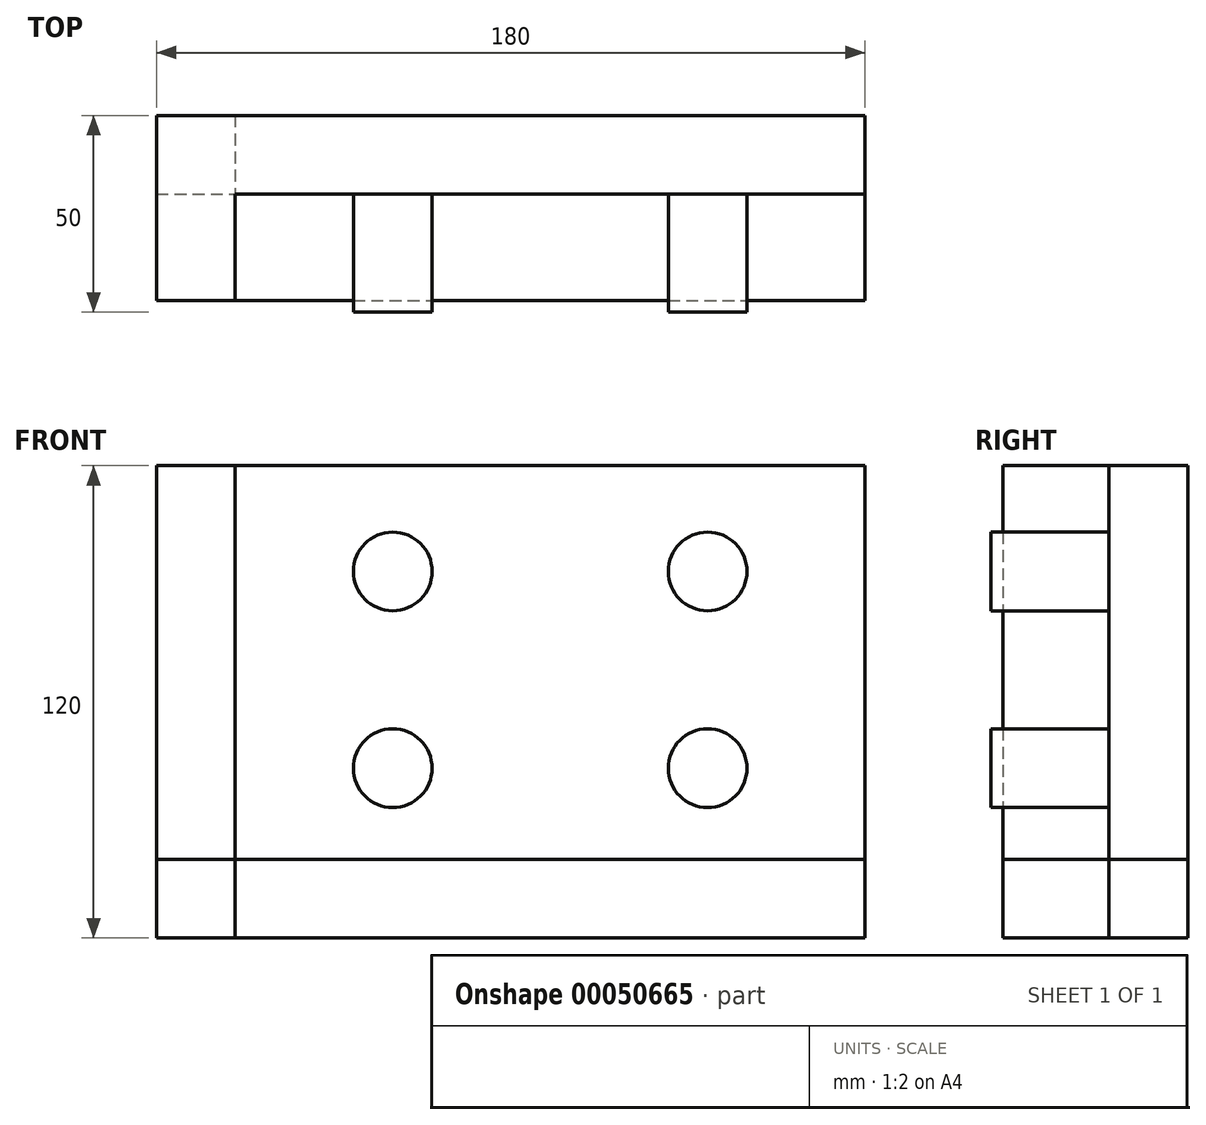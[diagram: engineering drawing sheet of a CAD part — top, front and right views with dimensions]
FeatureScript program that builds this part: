
annotation { "Feature Type Name" : "Feature", "Feature Type Description" : "" }
export const myFeature = defineFeature(function(context is Context, id is Id, definition is map)
    precondition{}
    {
        {
            var Q0;
            Q0=qCreatedBy(makeId("Front.planeOp"),FACE);
            var sketch = newSketch(context, id + "F0", { "sketchPlane" : qUnion([Q0])});
            skLineSegment(sketch, "E0.bottom", {"start": v(-80, 50) * mm, "end": v(80, 50) * mm});
            skLineSegment(sketch, "E0.top", {"start": v(-80, -50) * mm, "end": v(80, -50) * mm});
            skLineSegment(sketch, "E0.left", {"start": v(-80, 50) * mm, "end": v(-80, -50) * mm});
            skLineSegment(sketch, "E0.right", {"start": v(80, 50) * mm, "end": v(80, -50) * mm});
            skSolve(sketch);
        }
        {
            var Q0;
            Q0=makeQuery(id+"F0.imprint","IMPRINT",FACE,{"disambiguationData":[TD([[makeQuery(id+"F0.imprint","IMPRINT",EDGE,{"derivedFrom":sQuery(id+"F0.wireOp",EDGE,"E0.bottom")}),-1.0]])]});
            extrude(context, id + "F1", {"entities" : qUnion([Q0]), "oppositeDirection" : true, "depth" : 20 * mm});
        }
        {
            var Q0;
            Q0=qCreatedBy(makeId("Right.planeOp"),FACE);
            cPlane(context, id + "F2", {"entities" : qUnion([Q0]), "cplaneType" : CPlaneType.OFFSET, "offset" : 80 * mm, "oppositeDirection" : true, "width" : 150 * mm, "height" : 150 * mm});
        }
        {
            var Q0;
            Q0=qCreatedBy(id+"F2.planeOp",FACE);
            var sketch = newSketch(context, id + "F3", { "sketchPlane" : qUnion([Q0])});
            skLineSegment(sketch, "E1.bottom", {"start": v(-27, 50) * mm, "end": v(0, 50) * mm});
            skLineSegment(sketch, "E1.top", {"start": v(-27, -50) * mm, "end": v(0, -50) * mm});
            skLineSegment(sketch, "E1.left", {"start": v(-27, 50) * mm, "end": v(-27, -50) * mm});
            skLineSegment(sketch, "E1.right", {"start": v(0, 50) * mm, "end": v(0, -50) * mm});
            skSolve(sketch);
        }
        {
            var Q0;
            Q0=makeQuery(id+"F3.imprint","IMPRINT",FACE,{"disambiguationData":[TD([[makeQuery(id+"F3.imprint","IMPRINT",EDGE,{"derivedFrom":sQuery(id+"F3.wireOp",EDGE,"E1.bottom")}),-1.0]])]});
            extrude(context, id + "F4", {"entities" : qUnion([Q0]), "operationType" : NewBodyOperationType.ADD, "oppositeDirection" : true, "depth" : 20 * mm});
        }
        {
            var Q0;
            Q0=makeQuery(id+"F4.opExtrude","SWEPT_FACE",FACE,{"disambiguationData":[OSD([sQuery(id+"F3.wireOp",EDGE,"E1.left")])]});
            var Q1;
            Q1=makeQuery(id+"F4.opExtrude","SWEPT_FACE",FACE,{"disambiguationData":[OSD([sQuery(id+"F3.wireOp",EDGE,"E1.right")])]});
            extrude(context, id + "F5", {"entities" : qUnion([Q0, Q1]), "operationType" : NewBodyOperationType.ADD, "oppositeDirection" : true, "depth" : 20 * mm});
        }
        {
            var Q0;
            Q0=makeQuery(id+"F1.opExtrude","CAP_FACE",FACE,{"disambiguationData":[OSD([sQuery(id+"F0.wireOp",EDGE,"E0.bottom"),sQuery(id+"F0.wireOp",EDGE,"E0.top"),sQuery(id+"F0.wireOp",EDGE,"E0.left"),sQuery(id+"F0.wireOp",EDGE,"E0.right")])],"isStart":true});
            var sketch = newSketch(context, id + "F6", { "sketchPlane" : qUnion([Q0])});
            skCircle(sketch, "E2", {"center": v(-40, -26.85) * mm, "radius": 10 * mm});
            skCircle(sketch, "E3.0.1.0", {"center": v(-40, 23.15) * mm, "radius": 10 * mm});
            skCircle(sketch, "E3.1.0.0", {"center": v(40, -26.85) * mm, "radius": 10 * mm});
            skCircle(sketch, "E3.1.1.0", {"center": v(40, 23.15) * mm, "radius": 10 * mm});
            skLineSegment(sketch, "E3.direction1", {"start": v(-40, -26.85) * mm, "end": v(40, -26.85) * mm, "construction": true});
            skLineSegment(sketch, "E3.direction2", {"start": v(-40, -26.85) * mm, "end": v(-40, 23.15) * mm, "construction": true});
            skSolve(sketch);
        }
        {
            var Q0;
            Q0=qSketchRegion(id+"F6",true);
            extrude(context, id + "F7", {"entities" : qUnion([Q0]), "operationType" : NewBodyOperationType.ADD, "depth" : 30 * mm});
        }
        {
            var Q0;
            Q0=qCreatedBy(makeId("Top.planeOp"),FACE);
            cPlane(context, id + "F8", {"entities" : qUnion([Q0]), "cplaneType" : CPlaneType.OFFSET, "offset" : 50 * mm, "oppositeDirection" : true, "width" : 150 * mm, "height" : 150 * mm});
        }
        {
            var Q0;
            Q0=qCreatedBy(id+"F8.planeOp",FACE);
            var sketch = newSketch(context, id + "F9", { "sketchPlane" : qUnion([Q0])});
            skLineSegment(sketch, "E4.bottom", {"start": v(-80, 0) * mm, "end": v(80, 0) * mm});
            skLineSegment(sketch, "E4.top", {"start": v(-80, -27) * mm, "end": v(80, -27) * mm});
            skLineSegment(sketch, "E4.left", {"start": v(-80, 0) * mm, "end": v(-80, -27) * mm});
            skLineSegment(sketch, "E4.right", {"start": v(80, 0) * mm, "end": v(80, -27) * mm});
            skSolve(sketch);
        }
        {
            var Q0;
            Q0=makeQuery(id+"F9.imprint","IMPRINT",FACE,{"disambiguationData":[TD([[makeQuery(id+"F9.imprint","IMPRINT",EDGE,{"derivedFrom":sQuery(id+"F9.wireOp",EDGE,"E4.bottom")}),-1.0]])]});
            extrude(context, id + "F10", {"entities" : qUnion([Q0]), "oppositeDirection" : true, "depth" : 20 * mm});
        }
        {
            var Q0;
            Q0=makeQuery(id+"F10.opExtrude","SWEPT_FACE",FACE,{"disambiguationData":[OSD([sQuery(id+"F9.wireOp",EDGE,"E4.bottom")])]});
            var Q1;
            Q1=makeQuery(id+"F1.opExtrude","CAP_FACE",FACE,{"disambiguationData":[OSD([sQuery(id+"F0.wireOp",EDGE,"E0.bottom"),sQuery(id+"F0.wireOp",EDGE,"E0.top"),sQuery(id+"F0.wireOp",EDGE,"E0.left"),sQuery(id+"F0.wireOp",EDGE,"E0.right")])],"isStart":false});
            extrude(context, id + "F11", {"entities" : qUnion([Q0]), "endBound" : BoundingType.UP_TO_SURFACE, "endBoundEntityFace" : qUnion([Q1]), "depth" : 25 * mm});
        }
        {
            var Q0;
            Q0=makeQuery(id+"F10.opExtrude","SWEPT_FACE",FACE,{"disambiguationData":[OSD([sQuery(id+"F9.wireOp",EDGE,"E4.left")])]});
            var Q1;
            {var subQ0=sQuery(id+"F3.wireOp",EDGE,"E1.right");Q1=makeQuery(id+"F5.boolean.opBoolean","MERGE",FACE,{"derivedFrom":[makeQuery(id+"F4.opExtrude","CAP_FACE",FACE,{"disambiguationData":[OSD([sQuery(id+"F3.wireOp",EDGE,"E1.bottom"),sQuery(id+"F3.wireOp",EDGE,"E1.top"),sQuery(id+"F3.wireOp",EDGE,"E1.left"),subQ0])],"isStart":false}),makeQuery(id+"F5.opExtrude","SWEPT_FACE",FACE,{"disambiguationData":[OSD([subQ0]),TDD([makeQuery(id+"F4.opExtrude","CAP_EDGE",EDGE,{"disambiguationData":[OSD([subQ0])],"isStart":false})])]})]});}
            extrude(context, id + "F12", {"entities" : qUnion([Q0]), "endBound" : BoundingType.UP_TO_SURFACE, "endBoundEntityFace" : qUnion([Q1]), "depth" : 25 * mm});
        }
        {
            var Q0;
            Q0=makeQuery(id+"F11.opExtrude","SWEPT_FACE",FACE,{"disambiguationData":[OSD([sQuery(id+"F9.wireOp",EDGE,"E4.bottom"),sQuery(id+"F9.wireOp",EDGE,"E4.left")])]});
            var Q1;
            {var subQ0=sQuery(id+"F3.wireOp",EDGE,"E1.right");Q1=makeQuery(id+"F5.boolean.opBoolean","MERGE",FACE,{"derivedFrom":[makeQuery(id+"F4.opExtrude","CAP_FACE",FACE,{"disambiguationData":[OSD([sQuery(id+"F3.wireOp",EDGE,"E1.bottom"),sQuery(id+"F3.wireOp",EDGE,"E1.top"),sQuery(id+"F3.wireOp",EDGE,"E1.left"),subQ0])],"isStart":false}),makeQuery(id+"F5.opExtrude","SWEPT_FACE",FACE,{"disambiguationData":[OSD([subQ0]),TDD([makeQuery(id+"F4.opExtrude","CAP_EDGE",EDGE,{"disambiguationData":[OSD([subQ0])],"isStart":false})])]})]});}
            extrude(context, id + "F13", {"entities" : qUnion([Q0]), "endBound" : BoundingType.UP_TO_SURFACE, "endBoundEntityFace" : qUnion([Q1]), "depth" : 25 * mm});
        }
    });
